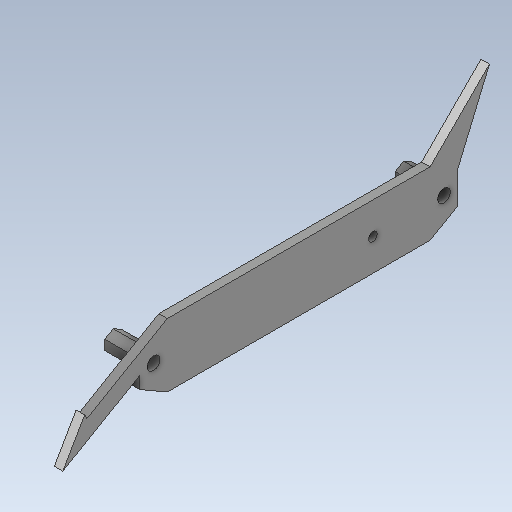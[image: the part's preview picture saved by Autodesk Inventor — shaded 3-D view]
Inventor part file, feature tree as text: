
AUTODESK INVENTOR PART (.ipt)
format: ipt  version: 2020 (Build 240168000, 168)  size: 161,280 bytes
history: native  units: in
note: dims shown in document units (in); Inventor stores cm internally (conversion verified against a paired STEP export)
features: other x3, extrude x2, sketch x2
ambient origin geometry x8: Origin, YZ Plane, XZ Plane, XY Plane, X Axis, Y Axis, Z Axis, Center Point
bodies: Solid1 (feature_tree)
feature tree (7):
  other  "HexWheelGuard.ipt"
  extrude  "Extrusion1"  Depth=0.315in
  extrude  "Extrusion2"  Depth=0.3937in
  other  "Solid1::HexWheelGuard.ipt"
  other  "TaggingFeature2"
  sketch  "Sketch1"  dims[d1=0.3937in d2=0.315in]
  sketch  "Sketch2"  dims[d3=60.0deg d4=1.4843in d5=0.0787in d6=0.3937in d7=0.0in d10=0.5906in d11=1.1024in d12=0.3937in d13=0.0in]
